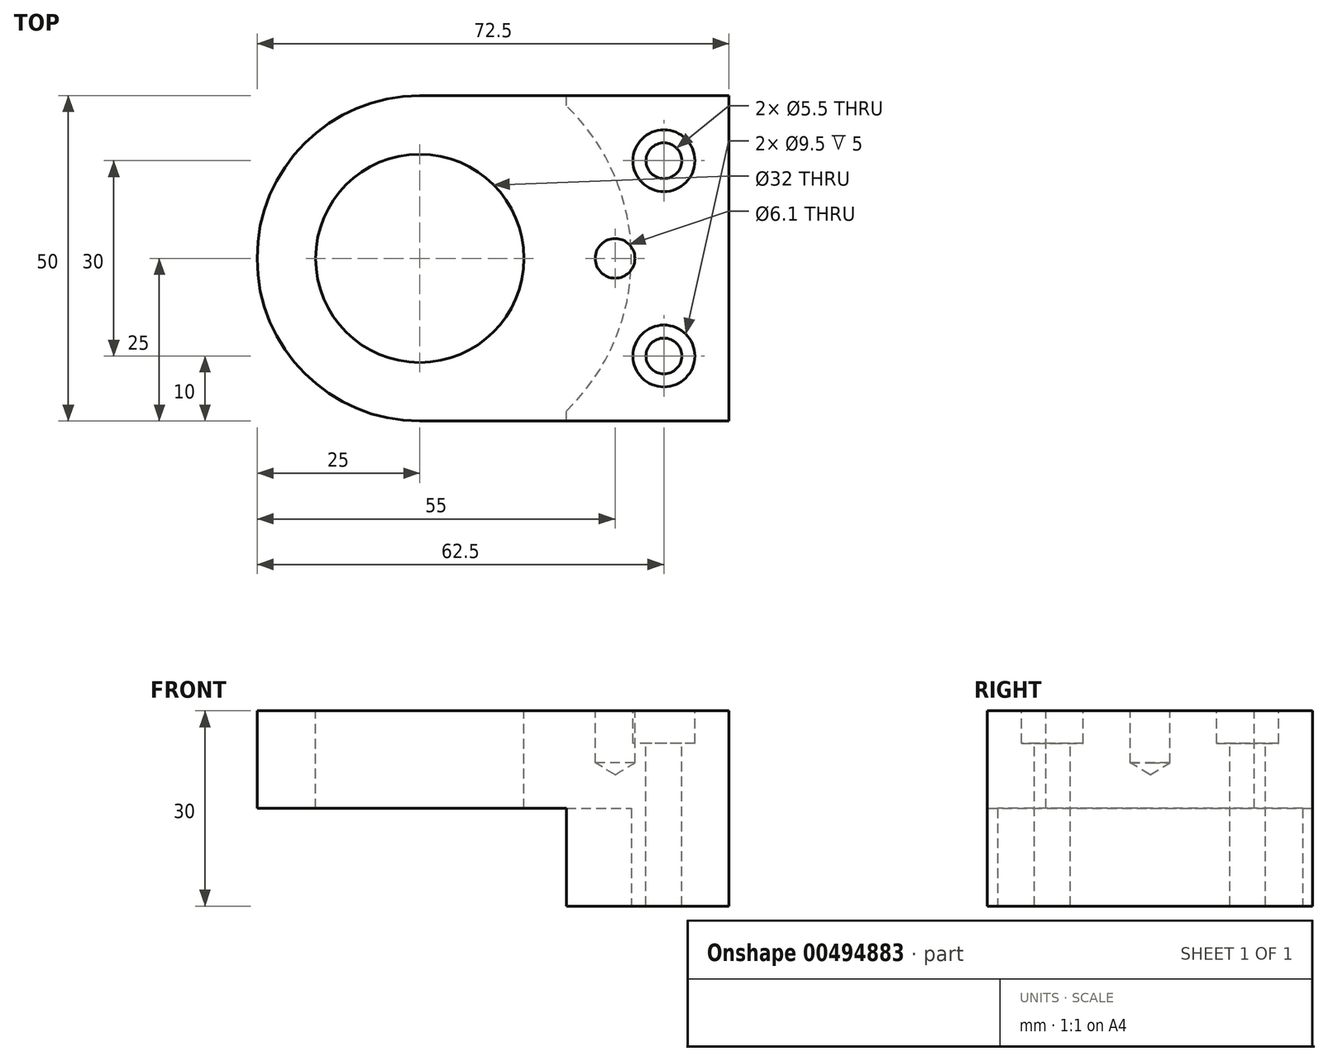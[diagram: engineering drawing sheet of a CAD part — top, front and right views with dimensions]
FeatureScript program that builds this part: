
annotation { "Feature Type Name" : "Feature", "Feature Type Description" : "" }
export const myFeature = defineFeature(function(context is Context, id is Id, definition is map)
    precondition{}
    {
        {
            var Q0;
            Q0=qCreatedBy(makeId("Top.planeOp"),FACE);
            var sketch = newSketch(context, id + "F0", { "sketchPlane" : qUnion([Q0])});
            skLineSegment(sketch, "E0.bottom", {"start": v(-55, 25) * mm, "end": v(17.5, 25) * mm});
            skLineSegment(sketch, "E0.top", {"start": v(-55, -25) * mm, "end": v(17.5, -25) * mm});
            skLineSegment(sketch, "E0.left", {"start": v(-55, 25) * mm, "end": v(-55, -25) * mm});
            skLineSegment(sketch, "E0.right", {"start": v(17.5, 25) * mm, "end": v(17.5, -25) * mm});
            skSolve(sketch);
        }
        {
            var Q0;
            Q0=qSketchRegion(id+"F0",true);
            extrude(context, id + "F1", {"entities" : qUnion([Q0]), "depth" : 30 * mm});
        }
        {
            var Q0;
            Q0=makeQuery(id+"F1.opExtrude","CAP_FACE",FACE,{"disambiguationData":[OSD([sQuery(id+"F0.wireOp",EDGE,"E0.bottom"),sQuery(id+"F0.wireOp",EDGE,"E0.top"),sQuery(id+"F0.wireOp",EDGE,"E0.left"),sQuery(id+"F0.wireOp",EDGE,"E0.right")])],"isStart":false});
            var sketch = newSketch(context, id + "F2", { "sketchPlane" : qUnion([Q0])});
            skCircle(sketch, "E1", {"center": v(-30, 0) * mm, "radius": 16 * mm});
            skSolve(sketch);
        }
        {
            var Q0;
            Q0=qSketchRegion(id+"F2",true);
            extrude(context, id + "F3", {"entities" : qUnion([Q0]), "operationType" : NewBodyOperationType.REMOVE, "endBound" : BoundingType.THROUGH_ALL, "oppositeDirection" : true, "depth" : 25 * mm});
        }
        {
            var Q0;
            Q0=makeQuery(id+"F1.opExtrude","CAP_FACE",FACE,{"disambiguationData":[OSD([sQuery(id+"F0.wireOp",EDGE,"E0.bottom"),sQuery(id+"F0.wireOp",EDGE,"E0.top"),sQuery(id+"F0.wireOp",EDGE,"E0.left"),sQuery(id+"F0.wireOp",EDGE,"E0.right")])],"isStart":false});
            var sketch = newSketch(context, id + "F4", { "sketchPlane" : qUnion([Q0])});
            skPoint(sketch, "E2", {"position": v(0, 0) * mm});
            skSolve(sketch);
        }
        {
            var Q0;
            Q0=sQuery(id+"F4.wireOp",VERTEX,"E2");
            var Q1;
            Q1=makeQuery(id+"F1.opExtrude","SWEPT_BODY",BODY,{"disambiguationData":[OSD([sQuery(id+"F0.wireOp",EDGE,"E0.bottom"),sQuery(id+"F0.wireOp",EDGE,"E0.top"),sQuery(id+"F0.wireOp",EDGE,"E0.left"),sQuery(id+"F0.wireOp",EDGE,"E0.right")])]});
            hole(context, id + "F5", {"style" : HoleStyle.SIMPLE, "endStyle" : HoleEndStyle.BLIND, "standardTappedOrClearance" : lookupTablePath({ "standard" : "ISO", "size" : "6.1", "type" : "Drilled" }), "standardBlindInLast" : lookupTablePath({ "standard" : "ISO", "size" : "6.1", "type" : "Drilled" }), "holeDiameter" : 6.1 * mm, "holeDepth" : 8 * mm, "isTappedThrough" : true, "tappedDepth" : 7.6 * mm, "tapClearance" : 3, "locations" : qUnion([Q0]), "scope" : qUnion([Q1])});
        }
        {
            var Q0;
            Q0=makeQuery(id+"F1.opExtrude","CAP_FACE",FACE,{"disambiguationData":[OSD([sQuery(id+"F0.wireOp",EDGE,"E0.bottom"),sQuery(id+"F0.wireOp",EDGE,"E0.top"),sQuery(id+"F0.wireOp",EDGE,"E0.left"),sQuery(id+"F0.wireOp",EDGE,"E0.right")])],"isStart":true});
            var sketch = newSketch(context, id + "F6", { "sketchPlane" : qUnion([Q0])});
            skCircle(sketch, "E3", {"center": v(-30, 0) * mm, "radius": 32.5 * mm});
            skSolve(sketch);
        }
        {
            var Q0;
            Q0=qSketchRegion(id+"F6",true);
            extrude(context, id + "F7", {"entities" : qUnion([Q0]), "operationType" : NewBodyOperationType.REMOVE, "oppositeDirection" : true, "depth" : 15 * mm});
        }
        {
            var Q0;
            Q0=makeQuery(id+"F1.opExtrude","SWEPT_EDGE",EDGE,{"disambiguationData":[OSD([sQuery(id+"F0.wireOp",EDGE,"E0.top"),sQuery(id+"F0.wireOp",EDGE,"E0.left")])]});
            var Q1;
            Q1=makeQuery(id+"F1.opExtrude","SWEPT_EDGE",EDGE,{"disambiguationData":[OSD([sQuery(id+"F0.wireOp",EDGE,"E0.bottom"),sQuery(id+"F0.wireOp",EDGE,"E0.left")])]});
            fillet(context, id + "F8", {"entities" : qUnion([Q0, Q1]), "radius" : 25 * mm, "tangentPropagation" : true, "allowEdgeOverflow" : false});
        }
        {
            var Q0;
            Q0=makeQuery(id+"F1.opExtrude","CAP_FACE",FACE,{"disambiguationData":[OSD([sQuery(id+"F0.wireOp",EDGE,"E0.bottom"),sQuery(id+"F0.wireOp",EDGE,"E0.top"),sQuery(id+"F0.wireOp",EDGE,"E0.left"),sQuery(id+"F0.wireOp",EDGE,"E0.right")])],"isStart":false});
            var sketch = newSketch(context, id + "F9", { "sketchPlane" : qUnion([Q0])});
            skPoint(sketch, "E4", {"position": v(7.5, -15) * mm});
            skPoint(sketch, "E5", {"position": v(7.5, 15) * mm});
            skSolve(sketch);
        }
        {
            var Q0;
            Q0=sQuery(id+"F9.wireOp",VERTEX,"E5");
            var Q1;
            Q1=sQuery(id+"F9.wireOp",VERTEX,"E4");
            var Q2;
            Q2=makeQuery(id+"F1.opExtrude","SWEPT_BODY",BODY,{"disambiguationData":[OSD([sQuery(id+"F0.wireOp",EDGE,"E0.bottom"),sQuery(id+"F0.wireOp",EDGE,"E0.top"),sQuery(id+"F0.wireOp",EDGE,"E0.left"),sQuery(id+"F0.wireOp",EDGE,"E0.right")])]});
            hole(context, id + "F10", {"style" : HoleStyle.C_BORE, "endStyle" : HoleEndStyle.THROUGH, "holeDiameter" : 5.5 * mm, "cBoreDiameter" : 9.5 * mm, "cBoreDepth" : 5 * mm, "isTappedThrough" : true, "tappedDepth" : 7.6 * mm, "tapClearance" : 3, "locations" : qUnion([Q0, Q1]), "scope" : qUnion([Q2])});
        }
        {
            var Q0;
            Q0=makeQuery(id+"F1.opExtrude","SWEPT_FACE",FACE,{"disambiguationData":[OSD([sQuery(id+"F0.wireOp",EDGE,"E0.bottom")])]});
            var sketch = newSketch(context, id + "F11", { "sketchPlane" : qUnion([Q0])});
            skLineSegment(sketch, "E6.bottom", {"start": v(9.23, 0) * mm, "end": v(7.5, 0) * mm});
            skLineSegment(sketch, "E6.top", {"start": v(9.23, 15) * mm, "end": v(7.5, 15) * mm});
            skLineSegment(sketch, "E6.left", {"start": v(9.23, 0) * mm, "end": v(9.23, 15) * mm});
            skLineSegment(sketch, "E6.right", {"start": v(7.5, 0) * mm, "end": v(7.5, 15) * mm});
            skSolve(sketch);
        }
        {
            var Q0;
            Q0=qSketchRegion(id+"F11",true);
            extrude(context, id + "F12", {"entities" : qUnion([Q0]), "operationType" : NewBodyOperationType.REMOVE, "endBound" : BoundingType.THROUGH_ALL, "oppositeDirection" : true, "depth" : 25 * mm});
        }
    });
